# Revit family: Тактильная керамическая плитка конус линейное расположение
name_source: partatom
category: Оборудование
revit_build: Autodesk Revit 2017 (Build: 20160225_1515(x64)
units: mm (PartAtom-declared; Revit-internal decimal feet)

## family parameters
Общий = Да
Основа = Грань
При загрузке вырезать с полостями = Да
Размер круглого соединителя = Использовать диаметр
Тип детали = Нормальный
Точка расчета площади = Нет

## types (2) — shared parameters
ADSK_Наименование = Тактильная керамическая плитка конус/линейное расположение
ADSK_Размер_Высота рифа = 5 мм
ADSK_Размер_Габариты = 300Х300
ADSK_Размер_Длина = 300 мм
ADSK_Размер_Толщина = 10 мм
ADSK_Размер_Ширина = 300 мм
ADSK_Тип рифов = Конусообразные рифы, линейное расположение
URL = http://tiflocentre.ru
Изготовитель = ТИФЛОЦЕНТР «ВЕРТИКАЛЬ»
Применение = Помещение
Стоимость = 1551 $
zero-valued in all types: Отметка по умолчанию

## per-type parameters (varying)
| type | ADSK_Код изделия | ADSK_Материал наименование | ADSK_Материал плитки | Описание |
| Тактильная керамическая плитка конус/линейное расположение_Желтая | 10684-ZH | Керамика, цвет желтый | Вертикаль_Керамическая плитка_Желтый | Специалистами Тифлоцентра «Вертикаль» была разработана и изготовлена серия тактильной керамической плитки, которая соответствует всем российским стандартам. Такая плитка предназначена для укладки внутри помещений с высокой проходимостью. Рифы, расположенные в линейном порядке, информируют незрячего человека о преодолимых препятствиях на пути следования. Желтый цвет плитки - отличный контраст к темной поверхности для слабовидящих людей. 
Благодаря одинаковой структуре с керамогранитным покрытием, при монтаже такая плитка выглядит как законченное решение
Обладает антивандальными свойствами, поэтому отлично подходит для мест с большой проходимостью (вокзалы, аэропорты, метро)
Имеет универсальный размер – 300х300, подходящий большинству керамогранитных плит
Высокая прочность и долговечность покрытия обуславливаются толщиной керамической плитки – 10 мм
Легко поддается санитарной обработке, не теряя при этом своего первоначального вида |
| Тактильная керамическая плитка конус/линейный_Черная | 10684-CH | Керамика, цвет черный | ВертикальКерамическая плитка_Черный | Специалистами Тифлоцентра «Вертикаль» была разработана и изготовлена серия тактильной керамической плитки, которая соответствует всем российским стандартам. Такая плитка предназначена для укладки внутри помещений с высокой проходимостью. Конусообразные рифы в линейном порядке информируют незрячего человека о преодолимом препятствии на пути, а черный цвет является незаменимым контрастом на светлой поверхности для слабовидящих людей. 
Благодаря одинаковой структуре с керамогранитным покрытием, при монтаже такая плитка выглядит как законченное решение
Обладает антивандальными свойствами, поэтому отлично подходит для мест с большой проходимостью (вокзалы, аэропорты, метро)
Имеет универсальный размер – 300х300, подходящий большинству керамогранитных плит
Высокая прочность и долговечность покрытия обуславливаются толщиной керамической плитки – 10 мм
Легко поддается санитарной обработке, не теряя при этом своего первоначального вида |
